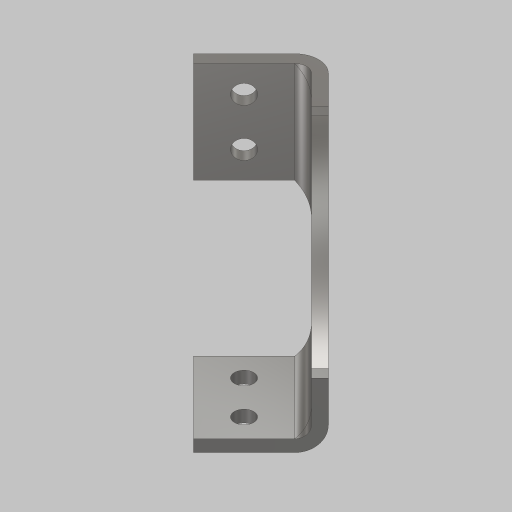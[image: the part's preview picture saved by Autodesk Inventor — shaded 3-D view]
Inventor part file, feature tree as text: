
AUTODESK INVENTOR PART (.ipt)
format: ipt  version: 2023.5 (Build 275446000, 446)  size: 294,912 bytes
history: native  units: in
note: dims shown in document units (in); Inventor stores cm internally (conversion verified against a paired STEP export)
features: projected_geometry x7, sketch x6, sheet_metal_op x5, hole x3, extrude x2, other x2
ambient origin geometry x8: Origin, YZ Plane, XZ Plane, XY Plane, X Axis, Y Axis, Z Axis, Center Point
bodies: Solid1 (feature_tree)
feature tree (25):
  extrude  "Extrusion1"  Depth=3.0in
  sheet_metal_op  "Flange1"
  hole  "Hole1"  [1 undecoded]
  hole  "Hole2"  [1 undecoded]
  hole  "Hole3"  [1 undecoded]
  sheet_metal_op  "Unfold1"
  extrude  "Extrusion2"  Depth=1.0in TaperAngle=90.0deg
  sheet_metal_op  "Refold1"
  sketch  "Sketch1"  dims[d0=0.75in d1=3.0in]
  sketch  "Sketch2"  dims[d2=0.125in d3=0.0in d4=45.0deg]
  other  "Plate1"
  sheet_metal_op  "Bend1"
  sheet_metal_op  "Corner1"
  sketch  "Sketch3"  dims[d5=0.125in d6=0.125in]
  sketch  "Sketch4"  dims[d7=0.0625in d8=0.25in]
  sketch  "Sketch5"  dims[d9=0.125in d10=1.0in d11=90.0deg d12=0.125in]
  sketch  "Sketch6"  dims[d13=0.5in d14=0.125in d15=0.125in d16=0.5in d17=0.201in d18=0.75in d19=0.385in d20=0.25in d21=0.5635in d22=0.125in d23=0.8108in d24=0.5in d25=0.201in d26=0.75in d27=0.375in d28=0.25in d29=0.5635in d30=1.0in d31=0.8108in d32=0.201in d33=0.75in d34=0.375in d35=0.25in d36=0.5635in d37=1.0in d38=0.8108in d39=0.311in d40=0.4375in d41=1.0in d42=0.0in d43=5.0in d45=0.5in d46=2.8125in]
  projected_geometry  "Projected Loop1"
  projected_geometry  "Projected Loop2"
  projected_geometry  "Projected Loop3"
  projected_geometry  "Projected Loop4"
  projected_geometry  "Project Cut Edges1"
  other  "Definition1"
  projected_geometry  "Project Cut Edges2"
  projected_geometry  "Project Cut Edges3"
note: 3 required parameter values undecoded (feature->parameter linkage not recoverable at this tier; creation-order binding heuristic only, values carry confidence <= 0.55)
